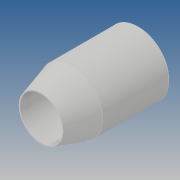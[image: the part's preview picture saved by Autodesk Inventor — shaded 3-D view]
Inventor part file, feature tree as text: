
AUTODESK INVENTOR PART (.ipt)
format: ipt  version: 2019 (Build 230136000, 136)  size: 117,760 bytes
history: native  units: mm
features: other x1, chamfer x1, sketch x1
ambient origin geometry x8: Origin, YZ Plane, XZ Plane, XY Plane, X Axis, Y Axis, Z Axis, Center Point
bodies: Solide1 (feature_tree)
feature tree (3):
  other  "Révolution1"
  chamfer  "Chanfrein1"  Distance=12.5mm
  sketch  "Esquisse1"
